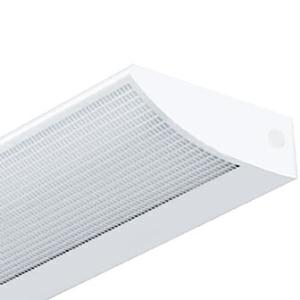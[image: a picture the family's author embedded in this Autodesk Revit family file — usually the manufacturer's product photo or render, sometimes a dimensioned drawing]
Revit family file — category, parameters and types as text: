
# Revit family: 3f_filippi_-_mira_par_dec_3f_filippi_-_1961_-_mira_par_led_de_4x12w_l675
name_source: partatom
category: Lighting Fixtures
units: mm (PartAtom-declared; Revit-internal decimal feet)

## family parameters
Cut with Voids When Loaded = No
Host = Face
Light Source = No
Part Type = Normal
Room Calculation Point = No
Round Connector Dimension = Use Diameter
Shared = No

## types (1)
- 3F Filippi - Mira Par Dec (1 x LED, 6699 lm, 56 W, 4000 K)
    Apparent Load = 56 VA
    Approval mark = ENEC
    CIE Flux Codes = 42 71 90 4 100
    Color Rendering = 80
    Color Temperature = 4000 K
    Control Gear = Electronic ballast
    Default Elevation = 1800 mm
    Description = ILLUMINOTECHNICAL
Luminous efficiency 100% (DLOR 4%, ULOR 96%).
Initial luminous flux of the luminaire 6699 lm.
Asymmetric direct-indirect distribution.
Average luminance <1000 cd/m² for radial angles >65°.
Beam angle: 108° - 110°.
Luminous efficacy 120 lm/W.
Lifetime (L93/B10): 30000 h. (tq+25°C)
Lifetime (L90/B10): 50000 h. (tq+25°C)
Lifetime (L85/B10): 80000 h. (tq+25°C)
Lifetime (L80/B10): 100000 h. (tq+25°C)
Sudden decreased luminous flux after 50000 hours: 0% (C0).
Photobiological safety in compliance with IEC/TR 62778: RG0 risk exempt, (IEC 62471).
In compliance with IEC/EN 62722-2-1 - IEC/EN 62717 standards.

SOURCE
4 linear LED modules 12W/840.
Energy efficiency class (UE 2019/2020 - UE 2019/2015): D.
CIE 13.3 Colour rendering index: CRI >80 (R9 <50%).
IES TM-30 Fidelity Index: Rf = 84 Rg = 95.
CCT nominal colour temperature 4000 K.
Colour initial tolerance (MacAdam): SDCM 3.

MECHANICAL
Housing in galvannealed steel, painted in white epoxy-polyester with reticular slots for high direct light emission.
Opal polycarbonate shielding film over the lower reticular zone.
Asymmetric flow recuperator, high efficiency, in specular aluminium with superficial titanium-magnesium treatment.
Opal acrylic upper diffuser.
Luminaire with limited surface temperature. - D - (EN 60598-2-24)
Dimensions: 675x230 mm, height 80 mm. Weight 2.675 kg.
IP40 protection degree.
Glow-wire test resistance 850°C.

ELECTRICAL
Halogen Free electronic wiring 230V-50/60Hz, power factor 0.95, THD <25%, constant output current, SELV, class I, 1 driver.
Power of the luminaire 56 W.
CE - IEC 60598-1 - EN 60598-1.
SAFE FLICKER: PstLM=<1 and SVM=<0.4 (IEC TR 61547-1 and IEC TR 63158), to ensure a more comfortable and safe light.
Luminaire compliant with EN 60598-2-22 for power supply from a centralised emergency system CPSS (Central Power Supply System), not incorporated in the luminaire - high risk areas excluded. The default power and flux are 100% in AC and 100% in DC.
Ambient temperature from 0°C to +25°C.
Temperature class T6 max 85°C.
Relative humidity UR: <85%.

INSTALLATION
Wall.
All accessories dedicated to this product are available on the Catalog and on our website www.3F-Filippi.com.

APPLICATIONS
Environments where a comfortable light is required. Luminaire for wall mounting, with an essential and modern design. Suitable for offices, conference rooms, managerial offices.

WARNING
Luminaire designed for disposal/recycling at end-of-life.
Replaceable (LED only) light source by a professional. Replaceable control gear by a professional.
    Height = 80 mm  [stored 0.262467 ft]
    Lamp = 1 x LED
    Lamp Light Flux = 6699 lm
    Lamp Power = 56 W
    Lamp count = 1
    Length = 675 mm
    Lifetime = 50000 h
    Luminous efficacy = 120 lm/W
    Manufacturer = 3F Filippi
    ModVariant = No
    Model = 3F Filippi - 1961 - MIRA PAR LED DE 4x12W L675
    Mounting Place = Wall
    Mounting Type = Surface mounted
    Number of Poles = 1
    OnlyDefault = Yes
    Power Factor = 1
    Product Name = 3F Filippi - Mira Par Dec
    Product group = wall-mounted luminaire
    ProductGroupID = 20
    Protection Class = Protection class I
    Protection Degree = IP 40
    RLX_Detail_Level = 1
    RLX_Emergency_Light_Flux = 0 lm
    RLX_Emergency_Type = 0
    RLX_Emergency_Type_DB = No
    RlxData = <blob elided: 59633 chars, md5=ab9afed5>
    Socket = socket
    Standby Power = 0 W
    System Light Flux = 6699 lm
    System Power = 56 W
    Type Comments = Product without accessories
    Type Image = 3ffilippi_mira_par.jpg
    URL = http://relux.com
    VarID = ---
    Voltage = 0 V
    Weight = 0.00 kg
    Width = 230 mm

note: [stored X ft] marks values corroborated as IEEE doubles in the binary element streams (Revit-internal decimal feet)

## geometry (parser evidence)
native form markers: Blend x4, Sweep x11
no freeform markers — native parametric forms only
